# Revit family: Downlight - Strip
name_source: partatom
category: Lighting Fixtures
revit_build: Autodesk Revit Architecture 2012 (Build: 20110210_1515)
units: mm (PartAtom-declared; Revit-internal decimal feet)

## types (4) — shared parameters
Assembly Code = D5020210
Ballast Number of Poles = 1
Color Filter = 16777215
Dimming Lamp Color Temperature Shift = <None>
Fixture Material = Glass - White, High Luminance
Light Box Material = Metal - Paint Finish - Ivory, Glossy
Light Source Symbol Size = 2' - 0"
Load Classification = Lighting - Dwelling Unit

## per-type parameters (varying)
| type | Apparent Load | Ballast Voltage | Emit from Line Length | Lamp | Light Length | Wattage Comments |
| 48" - 120V | 40 VA | 120 V | 3' - 10 1/2" | T-12 | 4' - 0" | 40 |
| 24" - 120V | 17 VA | 120 V | 1' - 10 1/2" | T-8 | 2' - 0" | 17 |
| 24" - 277V | 17 VA | 277 V | 1' - 10 1/2" | T-8 | 2' - 0" | 17 |
| 48" - 277V | 40 VA | 277 V | 3' - 10 1/2" | T-12 | 4' - 0" | 40 |

## geometry (parser evidence)
native form markers: Sweep x1
no freeform markers — native parametric forms only
